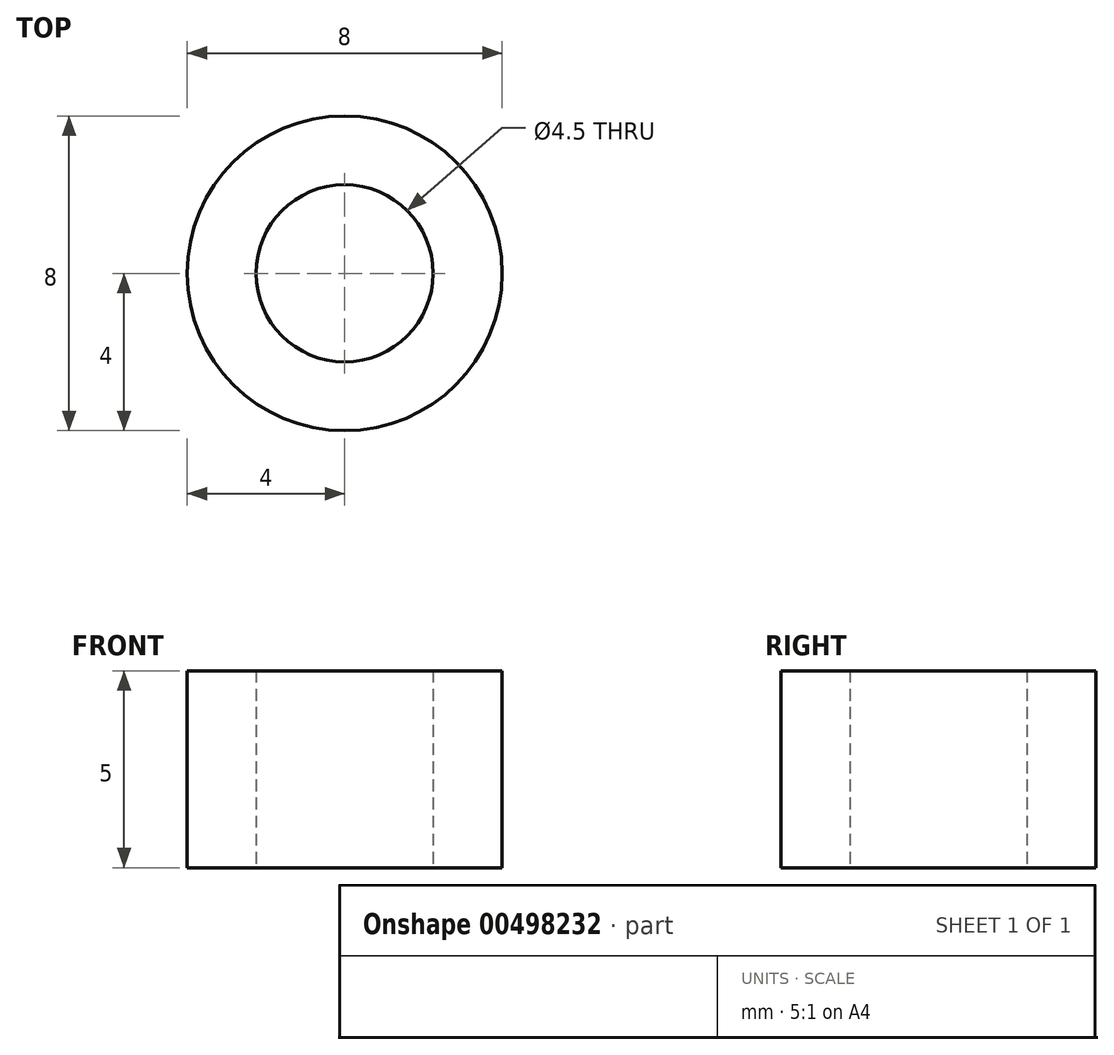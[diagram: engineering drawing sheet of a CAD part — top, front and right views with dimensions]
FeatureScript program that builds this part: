
annotation { "Feature Type Name" : "Feature", "Feature Type Description" : "" }
export const myFeature = defineFeature(function(context is Context, id is Id, definition is map)
    precondition{}
    {
        {
            var Q0;
            Q0=qCreatedBy(makeId("Top.planeOp"),FACE);
            var sketch = newSketch(context, id + "F0", { "sketchPlane" : qUnion([Q0])});
            skCircle(sketch, "E0", {"center": v(0, 0) * mm, "radius": 2.25 * mm});
            skCircle(sketch, "E1", {"center": v(0, 0) * mm, "radius": 4 * mm});
            skSolve(sketch);
        }
        {
            var Q0;
            Q0=makeQuery(id+"F0.imprint","IMPRINT",FACE,{"disambiguationData":[TD([[makeQuery(id+"F0.imprint","IMPRINT",EDGE,{"derivedFrom":sQuery(id+"F0.wireOp",EDGE,"E0")}),-1.0]])]});
            extrude(context, id + "F1", {"entities" : qUnion([Q0]), "depth" : 5 * mm});
        }
    });
